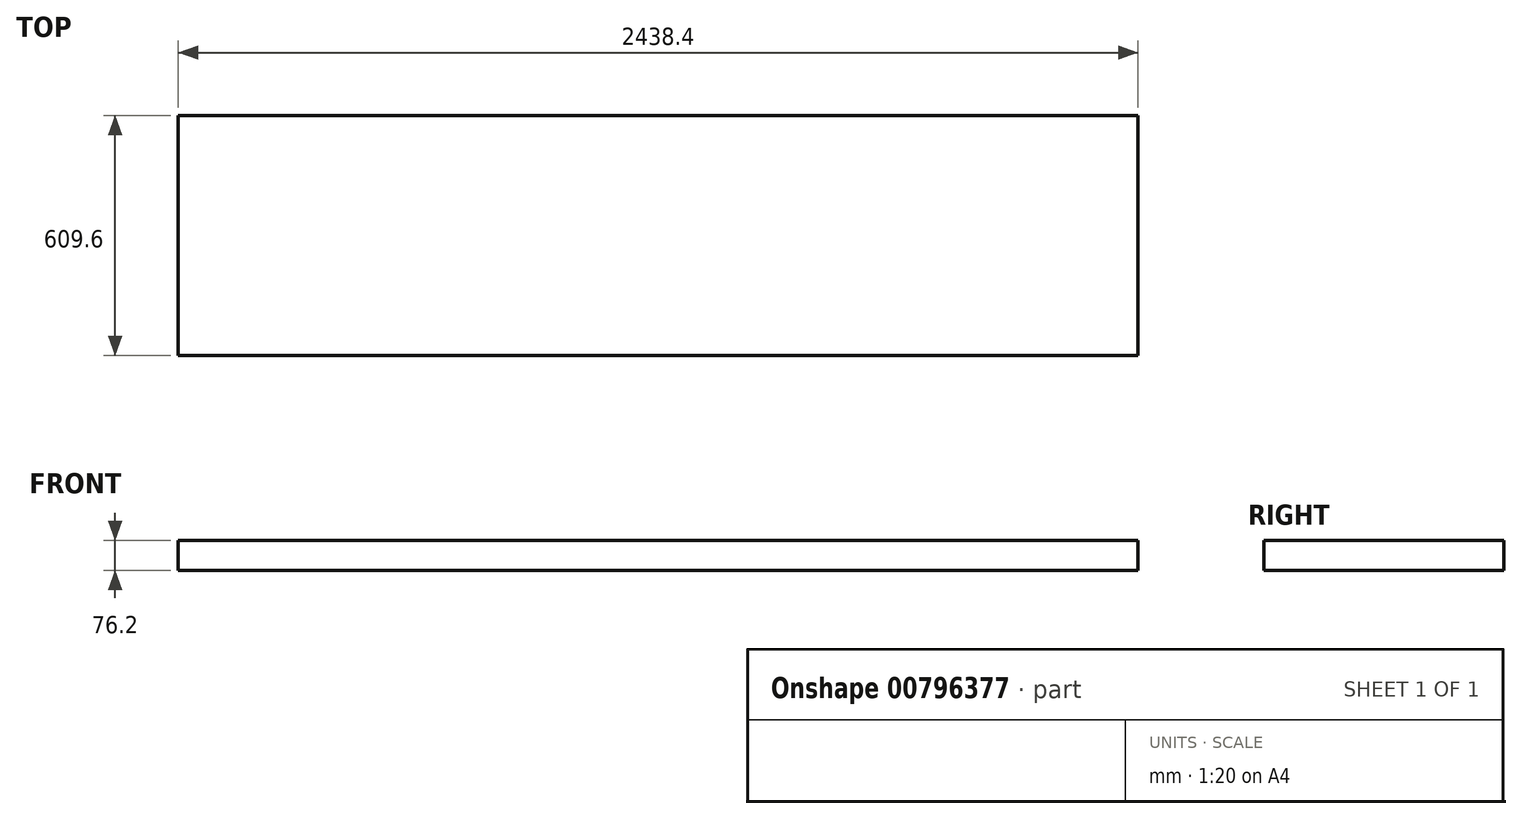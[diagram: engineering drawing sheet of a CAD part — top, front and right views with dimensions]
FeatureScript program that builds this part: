
annotation { "Feature Type Name" : "Feature", "Feature Type Description" : "" }
export const myFeature = defineFeature(function(context is Context, id is Id, definition is map)
    precondition{}
    {
        {
            var Q0;
            Q0=qCreatedBy(makeId("Top.planeOp"),FACE);
            var sketch = newSketch(context, id + "F0", { "sketchPlane" : qUnion([Q0])});
            skLineSegment(sketch, "E0.bottom", {"start": v(-1514.73, 310.96) * mm, "end": v(923.67, 310.96) * mm});
            skLineSegment(sketch, "E0.top", {"start": v(-1514.73, -298.64) * mm, "end": v(923.67, -298.64) * mm});
            skLineSegment(sketch, "E0.left", {"start": v(-1514.73, 310.96) * mm, "end": v(-1514.73, -298.64) * mm});
            skLineSegment(sketch, "E0.right", {"start": v(923.67, 310.96) * mm, "end": v(923.67, -298.64) * mm});
            skSolve(sketch);
        }
        {
            var Q0;
            Q0=makeQuery(id+"F0.imprint","IMPRINT",FACE,{"disambiguationData":[TD([[makeQuery(id+"F0.imprint","IMPRINT",EDGE,{"derivedFrom":sQuery(id+"F0.wireOp",EDGE,"E0.bottom")}),-1.0]])]});
            extrude(context, id + "F1", {"entities" : qUnion([Q0]), "depth" : 76.2 * mm, "offsetDistance" : 25.4 * mm});
        }
    });
